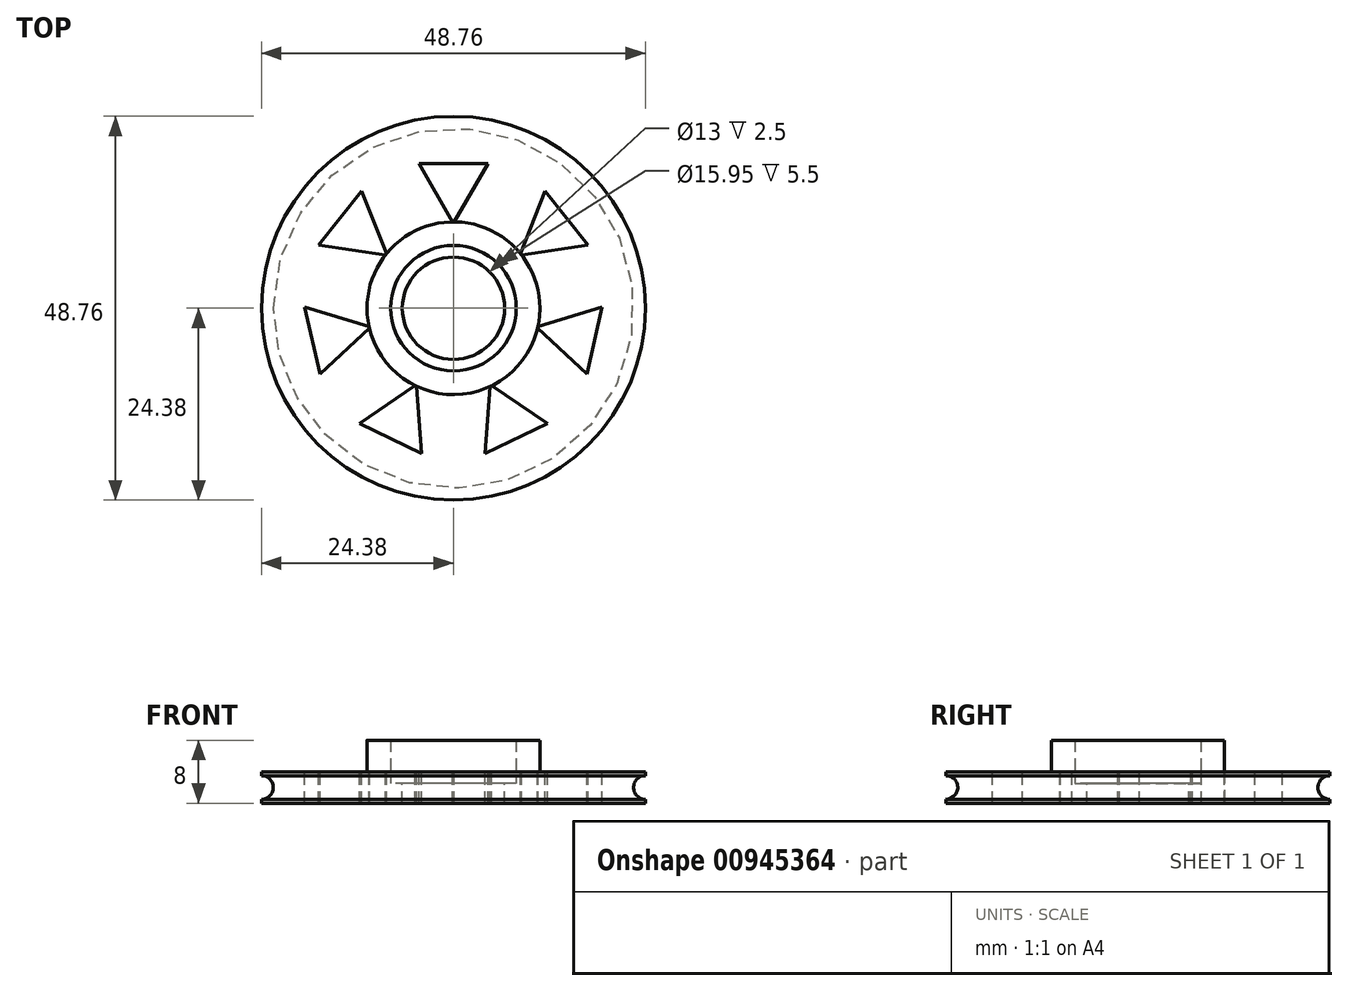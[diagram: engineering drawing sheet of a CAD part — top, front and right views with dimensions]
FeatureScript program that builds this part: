
annotation { "Feature Type Name" : "Feature", "Feature Type Description" : "" }
export const myFeature = defineFeature(function(context is Context, id is Id, definition is map)
    precondition{}
    {
        {
            var Q0;
            Q0=qCreatedBy(makeId("Top.planeOp"),FACE);
            var sketch = newSketch(context, id + "F0", { "sketchPlane" : qUnion([Q0])});
            skCircle(sketch, "E0", {"center": v(0, 0) * mm, "radius": 24.38 * mm});
            skSolve(sketch);
        }
        {
            var Q0;
            Q0=makeQuery(id+"F0.imprint","IMPRINT",FACE,{"disambiguationData":[TD([[makeQuery(id+"F0.imprint","IMPRINT",EDGE,{"derivedFrom":sQuery(id+"F0.wireOp",EDGE,"E0")}),1.0]])]});
            extrude(context, id + "F1", {"entities" : qUnion([Q0]), "depth" : 4 * mm, "offsetDistance" : 25.4 * mm});
        }
        {
            var Q0;
            Q0=makeQuery(id+"F1.opExtrude","CAP_FACE",FACE,{"disambiguationData":[OSD([sQuery(id+"F0.wireOp",EDGE,"E0"),sQuery(id+"F0.wireOp",EDGE,"n39IqKt5-bk1q-LU1x-fgod-8OyBNiFTd7FZ")])],"isStart":false});
            var sketch = newSketch(context, id + "F2", { "sketchPlane" : qUnion([Q0])});
            skCircle(sketch, "E1", {"center": v(0, 0) * mm, "radius": 7.97 * mm});
            skCircle(sketch, "E2.0", {"center": v(0, 0) * mm, "radius": 10.97 * mm});
            skCircle(sketch, "E3.cCircle", {"center": v(0, 15.86) * mm, "radius": 2.53 * mm, "construction": true});
            skLineSegment(sketch, "E3.0", {"start": v(-4.38, 18.38) * mm, "end": v(4.38, 18.38) * mm});
            skLineSegment(sketch, "E3.1", {"start": v(4.38, 18.38) * mm, "end": v(0, 10.8) * mm});
            skLineSegment(sketch, "E3.2", {"start": v(0, 10.8) * mm, "end": v(-4.38, 18.38) * mm});
            skPoint(sketch, "E3.0.midPoint", {"position": v(0, 18.38) * mm});
            skLineSegment(sketch, "E4.1.0", {"start": v(-17.1, 8.04) * mm, "end": v(-11.64, 14.88) * mm});
            skLineSegment(sketch, "E4.1.1", {"start": v(-11.64, 14.88) * mm, "end": v(-8.44, 6.73) * mm});
            skLineSegment(sketch, "E4.1.2", {"start": v(-8.44, 6.73) * mm, "end": v(-17.1, 8.04) * mm});
            skLineSegment(sketch, "E4.2.0", {"start": v(-16.95, -8.36) * mm, "end": v(-18.9, 0.18) * mm});
            skLineSegment(sketch, "E4.2.1", {"start": v(-18.9, 0.18) * mm, "end": v(-10.53, -2.4) * mm});
            skLineSegment(sketch, "E4.2.2", {"start": v(-10.53, -2.4) * mm, "end": v(-16.95, -8.36) * mm});
            skLineSegment(sketch, "E4.3.0", {"start": v(-4.03, -18.46) * mm, "end": v(-11.92, -14.66) * mm});
            skLineSegment(sketch, "E4.3.1", {"start": v(-11.92, -14.66) * mm, "end": v(-4.69, -9.73) * mm});
            skLineSegment(sketch, "E4.3.2", {"start": v(-4.69, -9.73) * mm, "end": v(-4.03, -18.46) * mm});
            skLineSegment(sketch, "E4.4.0", {"start": v(11.92, -14.66) * mm, "end": v(4.03, -18.46) * mm});
            skLineSegment(sketch, "E4.4.1", {"start": v(4.03, -18.46) * mm, "end": v(4.69, -9.73) * mm});
            skLineSegment(sketch, "E4.4.2", {"start": v(4.69, -9.73) * mm, "end": v(11.92, -14.66) * mm});
            skLineSegment(sketch, "E4.5.0", {"start": v(18.9, 0.18) * mm, "end": v(16.95, -8.36) * mm});
            skLineSegment(sketch, "E4.5.1", {"start": v(16.95, -8.36) * mm, "end": v(10.53, -2.4) * mm});
            skLineSegment(sketch, "E4.5.2", {"start": v(10.53, -2.4) * mm, "end": v(18.9, 0.18) * mm});
            skLineSegment(sketch, "E4.6.0", {"start": v(11.64, 14.88) * mm, "end": v(17.1, 8.04) * mm});
            skLineSegment(sketch, "E4.6.1", {"start": v(17.1, 8.04) * mm, "end": v(8.44, 6.73) * mm});
            skLineSegment(sketch, "E4.6.2", {"start": v(8.44, 6.73) * mm, "end": v(11.64, 14.88) * mm});
            skSolve(sketch);
        }
        {
            var Q0;
            {var subQ0=sQuery(id+"F2.wireOp",EDGE,"E4.6.2");var subQ1=sQuery(id+"F2.wireOp",EDGE,"E2.0");var subQ2=makeQuery(id+"F2.imprint","INTERSECT",VERTEX,{"derivedFrom":[subQ1,subQ0]});Q0=makeQuery(id+"F2.imprint","IMPRINT",FACE,{"disambiguationData":[TD([[makeQuery(id+"F2.imprint","IMPRINT",EDGE,{"disambiguationData":[TD([[subQ2,1.0]])],"derivedFrom":subQ1}),1.0]])]});}
            var Q1;
            {var subQ0=sQuery(id+"F2.wireOp",EDGE,"E3.1");var subQ1=sQuery(id+"F2.wireOp",EDGE,"E2.0");var subQ2=makeQuery(id+"F2.imprint","INTERSECT",VERTEX,{"derivedFrom":[subQ1,subQ0]});Q1=makeQuery(id+"F2.imprint","IMPRINT",FACE,{"disambiguationData":[TD([[makeQuery(id+"F2.imprint","IMPRINT",EDGE,{"disambiguationData":[TD([[subQ2,-1.0]])],"derivedFrom":subQ1}),1.0]])]});}
            var Q2;
            {var subQ0=sQuery(id+"F2.wireOp",EDGE,"E4.1.1");var subQ1=sQuery(id+"F2.wireOp",EDGE,"E2.0");var subQ2=makeQuery(id+"F2.imprint","INTERSECT",VERTEX,{"derivedFrom":[subQ1,subQ0]});Q2=makeQuery(id+"F2.imprint","IMPRINT",FACE,{"disambiguationData":[TD([[makeQuery(id+"F2.imprint","IMPRINT",EDGE,{"disambiguationData":[TD([[subQ2,-1.0]])],"derivedFrom":subQ1}),1.0]])]});}
            var Q3;
            {var subQ0=sQuery(id+"F2.wireOp",EDGE,"E4.2.1");var subQ1=sQuery(id+"F2.wireOp",EDGE,"E2.0");var subQ2=makeQuery(id+"F2.imprint","INTERSECT",VERTEX,{"derivedFrom":[subQ1,subQ0]});Q3=makeQuery(id+"F2.imprint","IMPRINT",FACE,{"disambiguationData":[TD([[makeQuery(id+"F2.imprint","IMPRINT",EDGE,{"disambiguationData":[TD([[subQ2,-1.0]])],"derivedFrom":subQ1}),1.0]])]});}
            var Q4;
            {var subQ0=sQuery(id+"F2.wireOp",EDGE,"E4.3.1");var subQ1=sQuery(id+"F2.wireOp",EDGE,"E2.0");var subQ2=makeQuery(id+"F2.imprint","INTERSECT",VERTEX,{"derivedFrom":[subQ1,subQ0]});Q4=makeQuery(id+"F2.imprint","IMPRINT",FACE,{"disambiguationData":[TD([[makeQuery(id+"F2.imprint","IMPRINT",EDGE,{"disambiguationData":[TD([[subQ2,-1.0]])],"derivedFrom":subQ1}),1.0]])]});}
            var Q5;
            {var subQ0=sQuery(id+"F2.wireOp",EDGE,"E4.4.1");var subQ1=sQuery(id+"F2.wireOp",EDGE,"E2.0");var subQ2=makeQuery(id+"F2.imprint","INTERSECT",VERTEX,{"derivedFrom":[subQ1,subQ0]});Q5=makeQuery(id+"F2.imprint","IMPRINT",FACE,{"disambiguationData":[TD([[makeQuery(id+"F2.imprint","IMPRINT",EDGE,{"disambiguationData":[TD([[subQ2,-1.0]])],"derivedFrom":subQ1}),1.0]])]});}
            var Q6;
            {var subQ0=sQuery(id+"F2.wireOp",EDGE,"E4.5.1");var subQ1=sQuery(id+"F2.wireOp",EDGE,"E2.0");var subQ2=makeQuery(id+"F2.imprint","INTERSECT",VERTEX,{"derivedFrom":[subQ1,subQ0]});Q6=makeQuery(id+"F2.imprint","IMPRINT",FACE,{"disambiguationData":[TD([[makeQuery(id+"F2.imprint","IMPRINT",EDGE,{"disambiguationData":[TD([[subQ2,-1.0]])],"derivedFrom":subQ1}),1.0]])]});}
            var Q7;
            Q7=makeQuery(id+"F2.imprint","IMPRINT",FACE,{"disambiguationData":[TD([[makeQuery(id+"F2.imprint","IMPRINT",EDGE,{"derivedFrom":sQuery(id+"F2.wireOp",EDGE,"E1")}),-1.0]])]});
            extrude(context, id + "F3", {"entities" : qUnion([Q0, Q1, Q2, Q3, Q4, Q5, Q6, Q7]), "operationType" : NewBodyOperationType.ADD, "depth" : 4 * mm, "offsetDistance" : 25.4 * mm});
        }
        {
            var Q0;
            Q0=makeQuery(id+"F3.boolean.opBoolean","SPLIT",FACE,{"disambiguationData":[TD([makeQuery(id+"F3.opExtrude","SWEPT_FACE",FACE,{"disambiguationData":[OSD([sQuery(id+"F2.wireOp",EDGE,"E1")])]})])],"derivedFrom":makeQuery(id+"F1.opExtrude","CAP_FACE",FACE,{"disambiguationData":[OSD([sQuery(id+"F0.wireOp",EDGE,"E0")])],"isStart":false})});
            var sketch = newSketch(context, id + "F4", { "sketchPlane" : qUnion([Q0])});
            skCircle(sketch, "E5", {"center": v(0, 0) * mm, "radius": 6.5 * mm});
            skSolve(sketch);
        }
        {
            var Q0;
            Q0=makeQuery(id+"F4.imprint","IMPRINT",FACE,{"disambiguationData":[TD([[makeQuery(id+"F4.imprint","IMPRINT",EDGE,{"derivedFrom":sQuery(id+"F4.wireOp",EDGE,"E5")}),1.0]])]});
            var Q1;
            Q1=makeQuery(id+"F4.imprint","IMPRINT",FACE,{"disambiguationData":[TD([[makeQuery(id+"F4.imprint","IMPRINT",EDGE,{"derivedFrom":makeQuery(id+"FgYK8jIepfClWtA_1.opExtrude","CAP_EDGE",EDGE,{"disambiguationData":[OSD([sQuery(id+"F8DXjnVyigKkjng_1.wireOp",EDGE,"EUjAMsCd-Zx2B-3j4q-cP5o-T3GrjTijNDqK")])],"isStart":false})}),1.0]])]});
            extrude(context, id + "F5", {"entities" : qUnion([Q0, Q1]), "operationType" : NewBodyOperationType.REMOVE, "oppositeDirection" : true, "depth" : 9 * mm, "offsetDistance" : 25.4 * mm});
        }
        {
            var Q0;
            Q0=qCreatedBy(makeId("Front.planeOp"),FACE);
            var sketch = newSketch(context, id + "F6", { "sketchPlane" : qUnion([Q0])});
            skCircle(sketch, "E6", {"center": v(-24.38, 2) * mm, "radius": 1.5 * mm});
            skLineSegment(sketch, "E7.bottom", {"start": v(-22.88, 0.65) * mm, "end": v(-25.02, 0.65) * mm});
            skLineSegment(sketch, "E7.top", {"start": v(-22.88, 3.35) * mm, "end": v(-25.02, 3.35) * mm});
            skLineSegment(sketch, "E7.left", {"start": v(-22.88, 0.65) * mm, "end": v(-22.88, 3.35) * mm});
            skLineSegment(sketch, "E7.right", {"start": v(-25.73, 1.35) * mm, "end": v(-25.73, 2.65) * mm});
            skLineSegment(sketch, "E8", {"start": v(0, 19.1) * mm, "end": v(0, -12.61) * mm, "construction": true});
            skLineSegment(sketch, "E9", {"start": v(-24.37, 3.35) * mm, "end": v(-22.88, 2) * mm});
            skLineSegment(sketch, "E10", {"start": v(-22.88, 2) * mm, "end": v(-24.38, 0.65) * mm});
            skLineSegment(sketch, "E11", {"start": v(-24.38, 0.65) * mm, "end": v(-24.37, 3.35) * mm});
            skSolve(sketch);
        }
        {
            var Q0;
            {var subQ0=sQuery(id+"F6.wireOp",EDGE,"E7.top");var subQ1=sQuery(id+"F6.wireOp",EDGE,"E6");var subQ2=makeQuery(id+"F6.imprint","INTERSECT",VERTEX,{"disambiguationData":[OD(0.0)],"derivedFrom":[subQ1,subQ0]});Q0=makeQuery(id+"F6.imprint","IMPRINT",FACE,{"disambiguationData":[TD([[makeQuery(id+"F6.imprint","IMPRINT",EDGE,{"disambiguationData":[TD([[subQ2,1.0]])],"derivedFrom":subQ1}),1.0]])]});}
            var Q1;
            {var subQ0=sQuery(id+"F6.wireOp",EDGE,"E7.bottom");var subQ1=sQuery(id+"F6.wireOp",EDGE,"E6");var subQ2=makeQuery(id+"F6.imprint","INTERSECT",VERTEX,{"disambiguationData":[OD(0.0)],"derivedFrom":[subQ1,subQ0]});Q1=makeQuery(id+"F6.imprint","IMPRINT",FACE,{"disambiguationData":[TD([[makeQuery(id+"F6.imprint","IMPRINT",EDGE,{"disambiguationData":[TD([[subQ2,-1.0]])],"derivedFrom":subQ1}),1.0]])]});}
            var Q2;
            {var subQ4=sQuery(id+"F6.wireOp",EDGE,"E7.right");Q2=makeQuery(id+"F6.imprint","IMPRINT",FACE,{"disambiguationData":[TD([[makeQuery(id+"F6.imprint","IMPRINT",EDGE,{"derivedFrom":subQ4}),-1.0]])]});}
            var Q3;
            {var subQ0=sQuery(id+"F6.wireOp",EDGE,"E9");Q3=makeQuery(id+"F6.imprint","IMPRINT",FACE,{"disambiguationData":[TD([[makeQuery(id+"F6.imprint","IMPRINT",EDGE,{"derivedFrom":subQ0}),1.0]])]});}
            var Q4;
            Q4=makeQuery(id+"F6.imprint","IMPRINT",FACE,{"disambiguationData":[TD([[makeQuery(id+"F6.imprint","IMPRINT",EDGE,{"derivedFrom":sQuery(id+"F6.wireOp",EDGE,"E9")}),-1.0]])]});
            var Q5;
            {var subQ0=sQuery(id+"F6.wireOp",EDGE,"E10");Q5=makeQuery(id+"F6.imprint","IMPRINT",FACE,{"disambiguationData":[TD([[makeQuery(id+"F6.imprint","IMPRINT",EDGE,{"derivedFrom":subQ0}),1.0]])]});}
            var Q6;
            Q6=sQuery(id+"F6.wireOp",EDGE,"E8");
            revolve(context, id + "F7", {"operationType" : NewBodyOperationType.REMOVE, "surfaceOperationType" : NewSurfaceOperationType.NEW, "entities" : qUnion([Q0, Q1, Q2, Q3, Q4, Q5]), "axis" : qUnion([Q6]), "revolveType" : RevolveType.FULL, "oppositeDirection" : true});
        }
        {
            var Q0;
            Q0=makeQuery(id+"F3.boolean.opBoolean","SPLIT",FACE,{"disambiguationData":[TD([makeQuery(id+"F3.opExtrude","SWEPT_FACE",FACE,{"disambiguationData":[OSD([sQuery(id+"F2.wireOp",EDGE,"E1")])]})])],"derivedFrom":makeQuery(id+"F1.opExtrude","CAP_FACE",FACE,{"disambiguationData":[OSD([sQuery(id+"F0.wireOp",EDGE,"E0")])],"isStart":false})});
            extrude(context, id + "F8", {"entities" : qUnion([Q0]), "operationType" : NewBodyOperationType.REMOVE, "flatOperationType" : FlatOperationType.REMOVE, "oppositeDirection" : true, "depth" : 1.5 * mm, "offsetDistance" : 25 * mm, "domain" : OperationDomain.MODEL});
        }
        {
            var Q0;
            {var subQ5=sQuery(id+"F2.wireOp",EDGE,"E4.3.0");Q0=makeQuery(id+"F2.imprint","IMPRINT",FACE,{"disambiguationData":[TD([[makeQuery(id+"F2.imprint","IMPRINT",EDGE,{"derivedFrom":subQ5}),-1.0]])]});}
            var Q1;
            {var subQ5=sQuery(id+"F2.wireOp",EDGE,"E4.2.0");Q1=makeQuery(id+"F2.imprint","IMPRINT",FACE,{"disambiguationData":[TD([[makeQuery(id+"F2.imprint","IMPRINT",EDGE,{"derivedFrom":subQ5}),-1.0]])]});}
            var Q2;
            {var subQ5=sQuery(id+"F2.wireOp",EDGE,"E4.1.0");Q2=makeQuery(id+"F2.imprint","IMPRINT",FACE,{"disambiguationData":[TD([[makeQuery(id+"F2.imprint","IMPRINT",EDGE,{"derivedFrom":subQ5}),-1.0]])]});}
            var Q3;
            {var subQ5=sQuery(id+"F2.wireOp",EDGE,"E3.0");Q3=makeQuery(id+"F2.imprint","IMPRINT",FACE,{"disambiguationData":[TD([[makeQuery(id+"F2.imprint","IMPRINT",EDGE,{"derivedFrom":subQ5}),-1.0]])]});}
            var Q4;
            {var subQ5=sQuery(id+"F2.wireOp",EDGE,"E4.6.0");Q4=makeQuery(id+"F2.imprint","IMPRINT",FACE,{"disambiguationData":[TD([[makeQuery(id+"F2.imprint","IMPRINT",EDGE,{"derivedFrom":subQ5}),-1.0]])]});}
            var Q5;
            {var subQ5=sQuery(id+"F2.wireOp",EDGE,"E4.5.0");Q5=makeQuery(id+"F2.imprint","IMPRINT",FACE,{"disambiguationData":[TD([[makeQuery(id+"F2.imprint","IMPRINT",EDGE,{"derivedFrom":subQ5}),-1.0]])]});}
            var Q6;
            {var subQ5=sQuery(id+"F2.wireOp",EDGE,"E4.4.0");Q6=makeQuery(id+"F2.imprint","IMPRINT",FACE,{"disambiguationData":[TD([[makeQuery(id+"F2.imprint","IMPRINT",EDGE,{"derivedFrom":subQ5}),-1.0]])]});}
            extrude(context, id + "F9", {"entities" : qUnion([Q0, Q1, Q2, Q3, Q4, Q5, Q6]), "operationType" : NewBodyOperationType.REMOVE, "oppositeDirection" : true, "depth" : 25 * mm, "offsetDistance" : 25 * mm});
        }
    });
